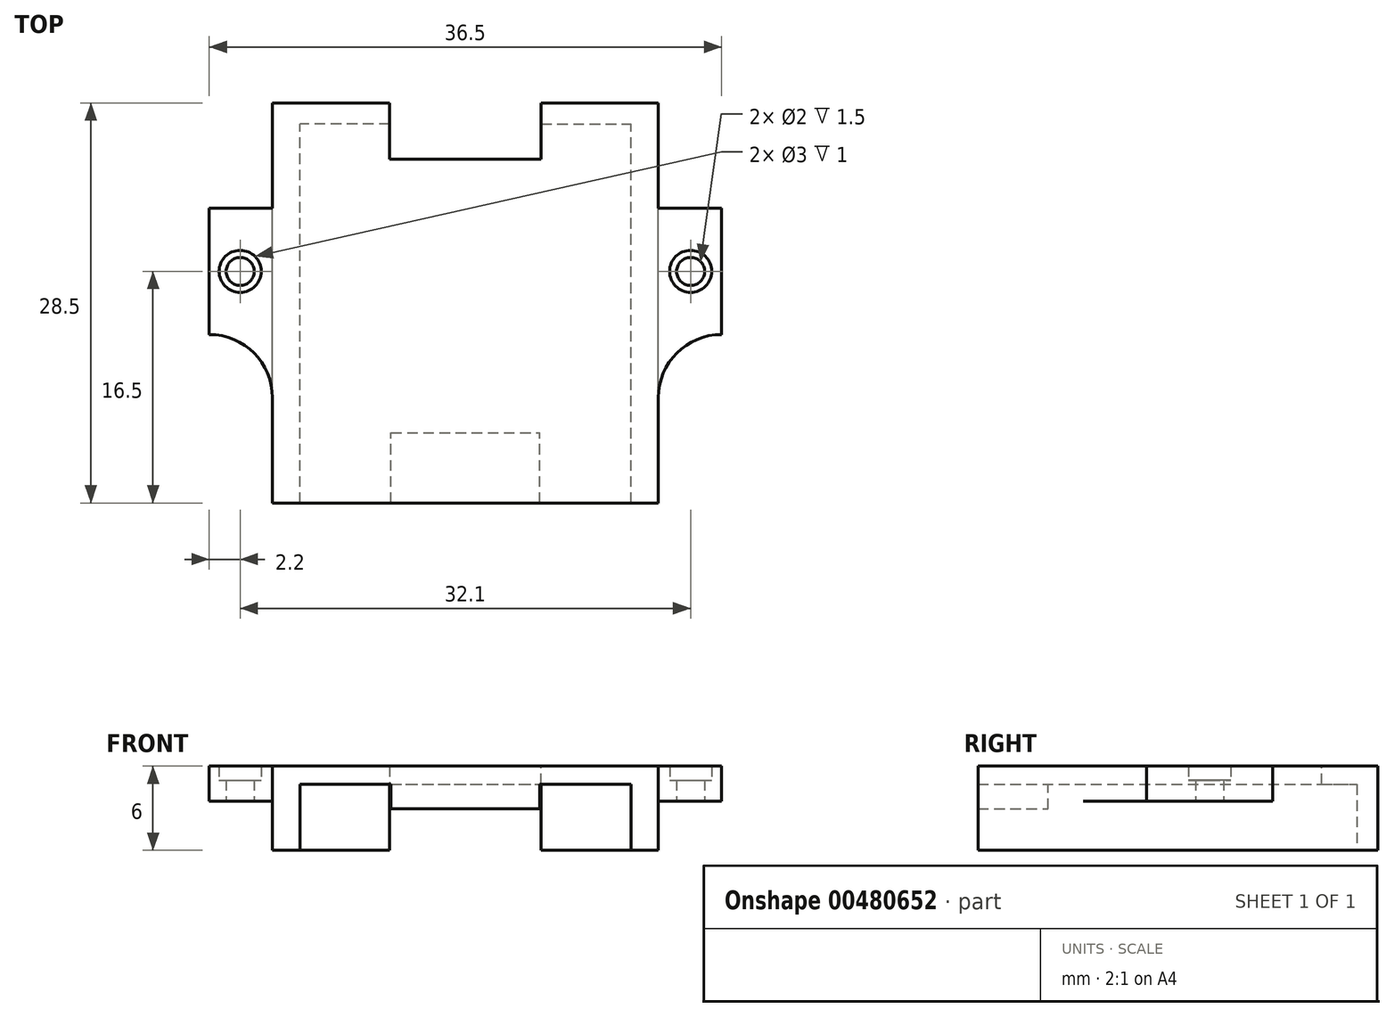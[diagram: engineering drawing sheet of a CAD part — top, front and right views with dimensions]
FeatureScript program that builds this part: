
annotation { "Feature Type Name" : "Feature", "Feature Type Description" : "" }
export const myFeature = defineFeature(function(context is Context, id is Id, definition is map)
    precondition{}
    {
        {
            var Q0;
            Q0=qCreatedBy(makeId("Front.planeOp"),FACE);
            var sketch = newSketch(context, id + "F0", { "sketchPlane" : qUnion([Q0])});
            skLineSegment(sketch, "E0.bottom", {"start": v(-13.75, 6) * mm, "end": v(13.75, 6) * mm});
            skLineSegment(sketch, "E0.top", {"start": v(-11.8, 4.7) * mm, "end": v(11.8, 4.7) * mm});
            skLineSegment(sketch, "E0.left", {"start": v(-11.8, 4.7) * mm, "end": v(-11.8, 0) * mm});
            skLineSegment(sketch, "E0.right", {"start": v(11.8, 4.7) * mm, "end": v(11.8, 0) * mm});
            skLineSegment(sketch, "E1", {"start": v(-13.75, 6) * mm, "end": v(-13.75, 0) * mm});
            skLineSegment(sketch, "E2", {"start": v(13.75, 6) * mm, "end": v(13.75, 0) * mm});
            skLineSegment(sketch, "E3", {"start": v(-13.75, 0) * mm, "end": v(-11.8, 0) * mm});
            skLineSegment(sketch, "E4", {"start": v(11.8, 0) * mm, "end": v(13.75, 0) * mm});
            skLineSegment(sketch, "E5", {"start": v(0, -9.15) * mm, "end": v(0, 16.75) * mm, "construction": true});
            skLineSegment(sketch, "E6", {"start": v(11.8, 0) * mm, "end": v(-11.8, 0) * mm, "construction": true});
            skSolve(sketch);
        }
        {
            var Q0;
            Q0=makeQuery(id+"F0.imprint","IMPRINT",FACE,{"disambiguationData":[TD([[makeQuery(id+"F0.imprint","IMPRINT",EDGE,{"derivedFrom":sQuery(id+"F0.wireOp",EDGE,"E0.bottom")}),-1.0]])]});
            extrude(context, id + "F1", {"entities" : qUnion([Q0]), "depth" : 28.5 * mm, "offsetDistance" : 25 * mm});
        }
        {
            var Q0;
            Q0=makeQuery(id+"F0.imprint","IMPRINT",FACE,{"disambiguationData":[TD([[makeQuery(id+"F0.imprint","IMPRINT",EDGE,{"derivedFrom":sQuery(id+"F0.wireOp",EDGE,"E0.bottom")}),-1.0]])]});
            var sketch = newSketch(context, id + "F2", { "sketchPlane" : qUnion([Q0])});
            skLineSegment(sketch, "E7.bottom", {"start": v(-13.6, 5) * mm, "end": v(13.6, 5) * mm});
            skLineSegment(sketch, "E8", {"start": v(-13.6, 5) * mm, "end": v(-13.6, 0) * mm});
            skLineSegment(sketch, "E9", {"start": v(13.6, 5) * mm, "end": v(13.6, 0) * mm});
            skLineSegment(sketch, "E10", {"start": v(13.6, 0) * mm, "end": v(-13.6, 0) * mm});
            skSolve(sketch);
        }
        {
            var Q0;
            {var subQ0=sQuery(id+"F0.wireOp",EDGE,"wRCYetyB-aeVf-4dhJ-iyEL-5ypZjPkGGYSX.bottom");Q0=makeQuery(id+"FSyTZdyDRPTgZKS_1.boolean.opBoolean","MERGE",FACE,{"derivedFrom":[makeQuery(id+"Fm8vXZimqr07P4D_1.boolean.opBoolean","MERGE",FACE,{"derivedFrom":[makeQuery(id+"F1.opExtrude","CAP_FACE",FACE,{"disambiguationData":[OSD([sQuery(id+"F0.wireOp",EDGE,"E0.bottom"),sQuery(id+"F0.wireOp",EDGE,"E0.top"),sQuery(id+"F0.wireOp",EDGE,"E0.left"),sQuery(id+"F0.wireOp",EDGE,"E0.right"),sQuery(id+"F0.wireOp",EDGE,"E1"),sQuery(id+"F0.wireOp",EDGE,"E2"),sQuery(id+"F0.wireOp",EDGE,"vC87NfnW-LpvK-T2V1-Tbur-f4zgu1OMRqjF"),sQuery(id+"F0.wireOp",EDGE,"NfAUiKOJ-rKyb-oKzE-H6jE-ePlwsaaBRTat"),sQuery(id+"F0.wireOp",EDGE,"E3"),sQuery(id+"F0.wireOp",EDGE,"E4"),sQuery(id+"F0.wireOp",EDGE,"RUeXVWWl-RcUU-cx36-pPEO-3SywNchYWJWJ"),sQuery(id+"F0.wireOp",EDGE,"6p0bEiKo-doeJ-IBKQ-lpXQ-GSclyybziE4s"),sQuery(id+"F0.wireOp",EDGE,"SEoIcKxP-fBzl-1vOu-vvdh-FIQF0VGQvLlq"),sQuery(id+"F0.wireOp",EDGE,"AVZkdrhp-E5xX-MGlL-SdQR-96536SC0HbCe"),sQuery(id+"F0.wireOp",EDGE,"885aa1ea-3d6b-49df-a24e-0734ddfef318.trimOffspring"),sQuery(id+"F0.wireOp",EDGE,"21f26947-704c-42b6-bcc5-de1c603d45f0.trimOffspring"),subQ0])],"isStart":true}),makeQuery(id+"Fm8vXZimqr07P4D_1.opExtrude","CAP_FACE",FACE,{"disambiguationData":[OSD([subQ0,sQuery(id+"F0.wireOp",EDGE,"wRCYetyB-aeVf-4dhJ-iyEL-5ypZjPkGGYSX.top"),sQuery(id+"F0.wireOp",EDGE,"wRCYetyB-aeVf-4dhJ-iyEL-5ypZjPkGGYSX.left"),sQuery(id+"F0.wireOp",EDGE,"wRCYetyB-aeVf-4dhJ-iyEL-5ypZjPkGGYSX.right")])],"isStart":true})]}),makeQuery(id+"FSyTZdyDRPTgZKS_1.opExtrude","CAP_FACE",FACE,{"disambiguationData":[OSD([sQuery(id+"F2.wireOp",EDGE,"E7.bottom"),sQuery(id+"F2.wireOp",EDGE,"E8"),sQuery(id+"F2.wireOp",EDGE,"E9"),sQuery(id+"F2.wireOp",EDGE,"E10")])],"isStart":true})]});}
            var sketch = newSketch(context, id + "F3", { "sketchPlane" : qUnion([Q0])});
            skLineSegment(sketch, "E11", {"start": v(-5.4, 0) * mm, "end": v(-5.4, 6) * mm});
            skLineSegment(sketch, "E12", {"start": v(0, 0) * mm, "end": v(5.4, 0) * mm});
            skLineSegment(sketch, "E13.bottom", {"start": v(-5.4, 6) * mm, "end": v(5.4, 6) * mm});
            skLineSegment(sketch, "E13.top", {"start": v(-5.4, 0) * mm, "end": v(5.4, 0) * mm});
            skLineSegment(sketch, "E13.left", {"start": v(-5.4, 6) * mm, "end": v(-5.4, 0) * mm});
            skLineSegment(sketch, "E13.right", {"start": v(5.4, 6) * mm, "end": v(5.4, 0) * mm});
            skLineSegment(sketch, "E14", {"start": v(-5.4, 0) * mm, "end": v(-11.8, 0) * mm});
            skLineSegment(sketch, "E15", {"start": v(-11.8, 0) * mm, "end": v(-11.8, 4.7) * mm});
            skLineSegment(sketch, "E16", {"start": v(-11.8, 4.7) * mm, "end": v(-5.4, 4.7) * mm});
            skLineSegment(sketch, "E17", {"start": v(-5.4, 4.7) * mm, "end": v(-5.4, 0) * mm});
            skLineSegment(sketch, "E18", {"start": v(0, -3.25) * mm, "end": v(0, 9.12) * mm, "construction": true});
            skLineSegment(sketch, "E19.MirrorCS", {"start": v(11.8, 0) * mm, "end": v(11.8, 4.7) * mm});
            skLineSegment(sketch, "E20.MirrorCS", {"start": v(5.4, 4.7) * mm, "end": v(5.4, 0) * mm});
            skLineSegment(sketch, "E21.MirrorCS", {"start": v(5.4, 0) * mm, "end": v(11.8, 0) * mm});
            skLineSegment(sketch, "E22.MirrorCS", {"start": v(11.8, 4.7) * mm, "end": v(5.4, 4.7) * mm});
            skSolve(sketch);
        }
        {
            var Q0;
            Q0=makeQuery(id+"F1.opExtrude","SWEPT_FACE",FACE,{"disambiguationData":[OSD([sQuery(id+"F0.wireOp",EDGE,"E0.bottom")])]});
            var sketch = newSketch(context, id + "F4", { "sketchPlane" : qUnion([Q0])});
            skPoint(sketch, "E23.endSnap0", {"position": v(0, -28.5) * mm});
            skCircle(sketch, "E24", {"center": v(-16.05, -12) * mm, "radius": 1 * mm, "construction": true});
            skLineSegment(sketch, "E25", {"start": v(-18.25, -7.5) * mm, "end": v(-13.75, -7.5) * mm});
            skLineSegment(sketch, "E26", {"start": v(-18.25, -7.5) * mm, "end": v(-18.25, -16.5) * mm});
            skLineSegment(sketch, "E27", {"start": v(-13.75, -21) * mm, "end": v(-13.75, -7.5) * mm});
            skLineSegment(sketch, "E28.MirrorCS", {"start": v(18.25, -7.5) * mm, "end": v(13.75, -7.5) * mm});
            skCircle(sketch, "E29.MirrorC", {"center": v(16.05, -12) * mm, "radius": 1 * mm, "construction": true});
            skLineSegment(sketch, "E30.MirrorCS", {"start": v(13.75, -21) * mm, "end": v(13.75, -7.5) * mm});
            skLineSegment(sketch, "E31.MirrorCS", {"start": v(18.25, -7.5) * mm, "end": v(18.25, -16.5) * mm});
            skArc(sketch, "E32.filletArc", {"start": v(-13.75, -21) * mm, "mid": v(-15.07, -17.82) * mm, "end": v(-18.25, -16.5) * mm});
            skLineSegment(sketch, "E33", {"start": v(0, -36.75) * mm, "end": v(0, 3.54) * mm, "construction": true});
            skArc(sketch, "E34.MirrorCS", {"start": v(13.75, -21) * mm, "mid": v(15.07, -17.82) * mm, "end": v(18.25, -16.5) * mm});
            skLineSegment(sketch, "E35", {"start": v(-16.05, -12) * mm, "end": v(16.05, -12) * mm, "construction": true});
            skLineSegment(sketch, "E36", {"start": v(0, -28.5) * mm, "end": v(0, -12) * mm, "construction": true});
            skLineSegment(sketch, "E37", {"start": v(-13.75, -7.5) * mm, "end": v(-13.75, 0) * mm, "construction": true});
            skLineSegment(sketch, "E38", {"start": v(-13.75, 0) * mm, "end": v(13.75, 0) * mm, "construction": true});
            skLineSegment(sketch, "E39", {"start": v(13.75, 0) * mm, "end": v(13.75, -7.5) * mm, "construction": true});
            skLineSegment(sketch, "E40", {"start": v(-13.75, -21) * mm, "end": v(-13.75, -28.5) * mm, "construction": true});
            skLineSegment(sketch, "E41", {"start": v(-13.75, -28.5) * mm, "end": v(13.75, -28.5) * mm, "construction": true});
            skLineSegment(sketch, "E42", {"start": v(13.75, -28.5) * mm, "end": v(13.75, -21) * mm, "construction": true});
            skSolve(sketch);
        }
        {
            var Q0;
            Q0=makeQuery(id+"F4.imprint","IMPRINT",FACE,{"disambiguationData":[TD([[makeQuery(id+"F4.imprint","IMPRINT",EDGE,{"derivedFrom":sQuery(id+"F4.wireOp",EDGE,"E25")}),-1.0]])]});
            var Q1;
            Q1=makeQuery(id+"F4.imprint","IMPRINT",FACE,{"disambiguationData":[TD([[makeQuery(id+"F4.imprint","IMPRINT",EDGE,{"derivedFrom":sQuery(id+"F4.wireOp",EDGE,"E28.MirrorCS")}),1.0]])]});
            extrude(context, id + "F5", {"entities" : qUnion([Q0, Q1]), "operationType" : NewBodyOperationType.ADD, "oppositeDirection" : true, "depth" : 2.5 * mm});
        }
        {
            var Q0;
            Q0=sQuery(id+"F4.wireOp",VERTEX,"E24.center");
            var Q1;
            Q1=sQuery(id+"F4.wireOp",VERTEX,"E29.MirrorC.center");
            var Q2;
            Q2=makeQuery(id+"F1.opExtrude","SWEPT_BODY",BODY,{"disambiguationData":[OSD([sQuery(id+"F0.wireOp",EDGE,"E0.bottom"),sQuery(id+"F0.wireOp",EDGE,"E0.top"),sQuery(id+"F0.wireOp",EDGE,"E0.left"),sQuery(id+"F0.wireOp",EDGE,"E0.right"),sQuery(id+"F0.wireOp",EDGE,"E1"),sQuery(id+"F0.wireOp",EDGE,"E2"),sQuery(id+"F0.wireOp",EDGE,"vC87NfnW-LpvK-T2V1-Tbur-f4zgu1OMRqjF"),sQuery(id+"F0.wireOp",EDGE,"NfAUiKOJ-rKyb-oKzE-H6jE-ePlwsaaBRTat"),sQuery(id+"F0.wireOp",EDGE,"E3"),sQuery(id+"F0.wireOp",EDGE,"E4"),sQuery(id+"F0.wireOp",EDGE,"RUeXVWWl-RcUU-cx36-pPEO-3SywNchYWJWJ"),sQuery(id+"F0.wireOp",EDGE,"6p0bEiKo-doeJ-IBKQ-lpXQ-GSclyybziE4s"),sQuery(id+"F0.wireOp",EDGE,"SEoIcKxP-fBzl-1vOu-vvdh-FIQF0VGQvLlq"),sQuery(id+"F0.wireOp",EDGE,"AVZkdrhp-E5xX-MGlL-SdQR-96536SC0HbCe"),sQuery(id+"F0.wireOp",EDGE,"885aa1ea-3d6b-49df-a24e-0734ddfef318.trimOffspring"),sQuery(id+"F0.wireOp",EDGE,"21f26947-704c-42b6-bcc5-de1c603d45f0.trimOffspring"),sQuery(id+"F0.wireOp",EDGE,"wRCYetyB-aeVf-4dhJ-iyEL-5ypZjPkGGYSX.bottom")])]});
            hole(context, id + "F6", {"style" : HoleStyle.C_BORE, "endStyle" : HoleEndStyle.THROUGH, "holeDiameter" : 2 * mm, "cBoreDiameter" : 3 * mm, "cBoreDepth" : 1 * mm, "isTappedThrough" : true, "tappedDepth" : 12 * mm, "tapClearance" : 3, "startFromSketch" : true, "locations" : qUnion([Q0, Q1]), "scope" : qUnion([Q2])});
        }
        {
            var Q0;
            {var subQ0=sQuery(id+"F3.wireOp",EDGE,"E13.bottom");Q0=makeQuery(id+"F3.imprint","IMPRINT",FACE,{"disambiguationData":[TD([[makeQuery(id+"F3.imprint","IMPRINT",EDGE,{"derivedFrom":subQ0}),1.0]])]});}
            extrude(context, id + "F7", {"entities" : qUnion([Q0]), "operationType" : NewBodyOperationType.REMOVE, "oppositeDirection" : true, "depth" : 4 * mm, "offsetDistance" : 25 * mm});
        }
        {
            var Q0;
            Q0=makeQuery(id+"F1.opExtrude","SWEPT_FACE",FACE,{"disambiguationData":[OSD([sQuery(id+"F0.wireOp",EDGE,"E0.top")])]});
            var sketch = newSketch(context, id + "F8", { "sketchPlane" : qUnion([Q0])});
            skLineSegment(sketch, "E43.bottom", {"start": v(-5.3, 28.5) * mm, "end": v(5.3, 28.5) * mm});
            skLineSegment(sketch, "E43.top", {"start": v(-5.3, 23.5) * mm, "end": v(5.3, 23.5) * mm});
            skLineSegment(sketch, "E43.left", {"start": v(-5.3, 28.5) * mm, "end": v(-5.3, 23.5) * mm});
            skLineSegment(sketch, "E43.right", {"start": v(5.3, 28.5) * mm, "end": v(5.3, 23.5) * mm});
            skSolve(sketch);
        }
        {
            var Q0;
            Q0 = qSketchRegion(id + "F8", true);
            extrude(context, id + "F9", {"entities" : qUnion([Q0]), "operationType" : NewBodyOperationType.ADD, "depth" : 1.75 * mm, "offsetDistance" : 25 * mm});
        }
        {
            var Q0;
            Q0=makeQuery(id+"F3.imprint","IMPRINT",FACE,{"disambiguationData":[TD([[makeQuery(id+"F3.imprint","IMPRINT",EDGE,{"derivedFrom":sQuery(id+"F3.wireOp",EDGE,"E14")}),-1.0]])]});
            var Q1;
            Q1=makeQuery(id+"F3.imprint","IMPRINT",FACE,{"disambiguationData":[TD([[makeQuery(id+"F3.imprint","IMPRINT",EDGE,{"derivedFrom":sQuery(id+"F3.wireOp",EDGE,"E19.MirrorCS")}),-1.0]])]});
            extrude(context, id + "F10", {"entities" : qUnion([Q0, Q1]), "operationType" : NewBodyOperationType.ADD, "oppositeDirection" : true, "depth" : 1.5 * mm, "offsetDistance" : 25 * mm});
        }
    });
